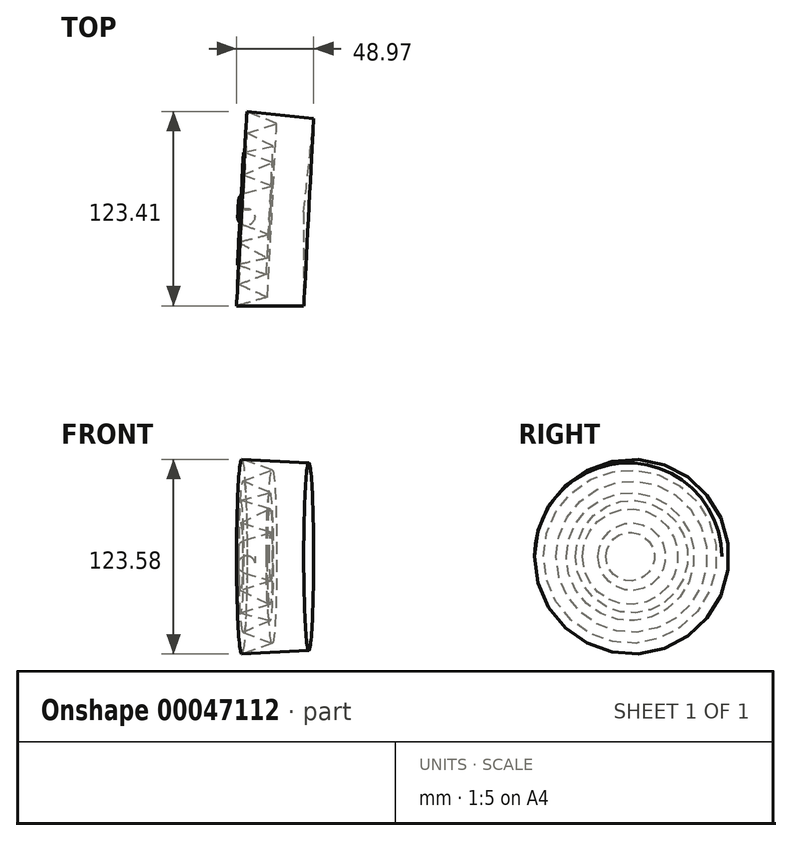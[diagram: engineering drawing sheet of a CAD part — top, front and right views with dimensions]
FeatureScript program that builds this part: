
annotation { "Feature Type Name" : "Feature", "Feature Type Description" : "" }
export const myFeature = defineFeature(function(context is Context, id is Id, definition is map)
    precondition{}
    {
        {
            var Q0;
            Q0=qCreatedBy(makeId("Top.planeOp"),FACE);
            var sketch = newSketch(context, id + "F0", { "sketchPlane" : qUnion([Q0])});
            skLineSegment(sketch, "E0", {"start": v(-38.38, 51.45) * mm, "end": v(-21.68, 45.3) * mm});
            skLineSegment(sketch, "E1", {"start": v(-21.68, 45.3) * mm, "end": v(-41.16, 40.33) * mm});
            skLineSegment(sketch, "E2", {"start": v(-41.16, 40.33) * mm, "end": v(-23, 30.32) * mm});
            skLineSegment(sketch, "E3", {"start": v(-23, 30.32) * mm, "end": v(-42.1, 26.05) * mm});
            skLineSegment(sketch, "E4", {"start": v(-42.1, 26.05) * mm, "end": v(-23.73, 20.12) * mm});
            skLineSegment(sketch, "E5", {"start": v(-23.73, 20.12) * mm, "end": v(-40.98, 13.63) * mm});
            skLineSegment(sketch, "E6", {"start": v(-40.98, 13.63) * mm, "end": v(-23, 5.66) * mm});
            skLineSegment(sketch, "E7", {"start": v(-23, 5.66) * mm, "end": v(-42.65, 0) * mm});
            skLineSegment(sketch, "E8", {"start": v(-42.65, 0) * mm, "end": v(0, 0) * mm});
            skArc(sketch, "E9", {"start": v(-38.38, 61.65) * mm, "mid": v(-41.94, 56.55) * mm, "end": v(-38.38, 51.45) * mm});
            skLineSegment(sketch, "E10", {"start": v(-38.38, 61.65) * mm, "end": v(0, 59.61) * mm});
            skLineSegment(sketch, "E11", {"start": v(0, 59.61) * mm, "end": v(0, 0) * mm});
            skSolve(sketch);
        }
        {
            var Q0;
            Q0 = qSketchRegion(id + "F0", true);
            var Q1;
            Q1=sQuery(id+"F0.wireOp",EDGE,"E10");
            revolve(context, id + "F1", {"entities" : qUnion([Q0]), "axis" : qUnion([Q1]), "revolveType" : RevolveType.FULL});
        }
    });
